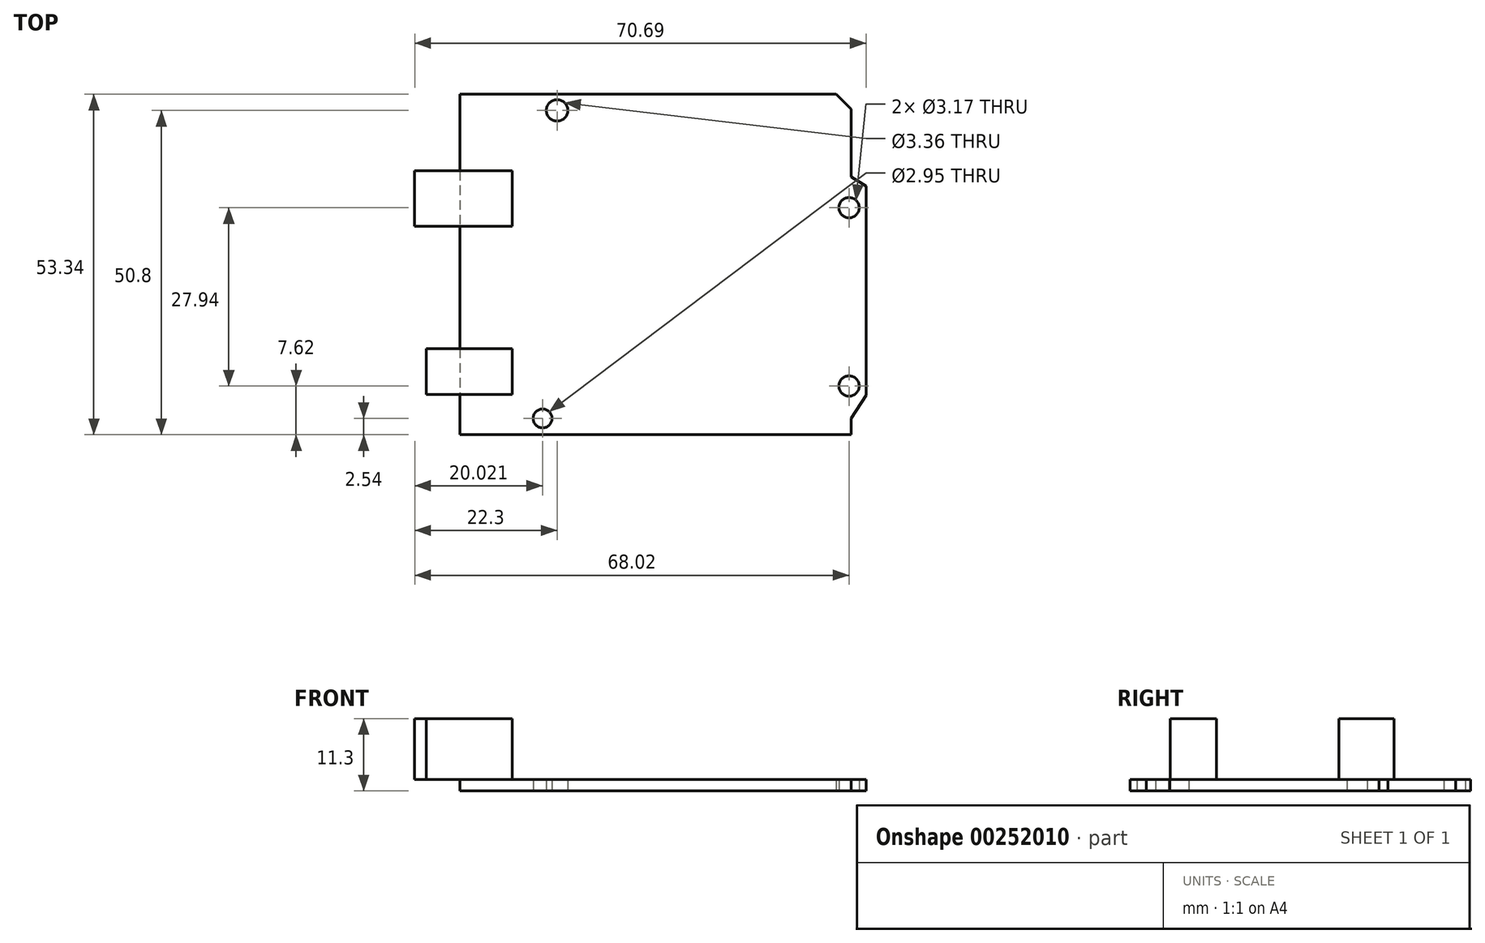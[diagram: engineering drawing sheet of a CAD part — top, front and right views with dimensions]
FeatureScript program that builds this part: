
annotation { "Feature Type Name" : "Feature", "Feature Type Description" : "" }
export const myFeature = defineFeature(function(context is Context, id is Id, definition is map)
    precondition{}
    {
        {
            var Q0;
            Q0=qCreatedBy(makeId("Top.planeOp"),FACE);
            var sketch = newSketch(context, id + "F0", { "sketchPlane" : qUnion([Q0])});
            skLineSegment(sketch, "E0", {"start": v(0, 0) * mm, "end": v(61.27, 0) * mm});
            skLineSegment(sketch, "E1", {"start": v(61.27, 0) * mm, "end": v(61.27, 2.54) * mm});
            skLineSegment(sketch, "E2", {"start": v(0, 53.34) * mm, "end": v(58.91, 53.34) * mm});
            skLineSegment(sketch, "E3", {"start": v(61.27, 50.98) * mm, "end": v(61.27, 40.38) * mm});
            skLineSegment(sketch, "E4", {"start": v(58.91, 53.34) * mm, "end": v(61.27, 50.98) * mm});
            skPoint(sketch, "E5", {"position": v(63.63, 38.97) * mm});
            skLineSegment(sketch, "E6", {"start": v(61.27, 40.38) * mm, "end": v(63.63, 38.97) * mm});
            skCircle(sketch, "E7", {"center": v(12.96, 2.54) * mm, "radius": 1.47 * mm});
            skCircle(sketch, "E8", {"center": v(15.24, 50.8) * mm, "radius": 1.68 * mm});
            skLineSegment(sketch, "E9", {"start": v(63.63, 38.97) * mm, "end": v(63.63, 6.2) * mm});
            skLineSegment(sketch, "E10", {"start": v(63.63, 6.2) * mm, "end": v(61.27, 2.54) * mm});
            skCircle(sketch, "E11", {"center": v(60.96, 35.56) * mm, "radius": 1.59 * mm});
            skCircle(sketch, "E12", {"center": v(60.96, 7.62) * mm, "radius": 1.59 * mm});
            skPoint(sketch, "E13.start.orphan", {"position": v(10.6, 2.95) * mm});
            skLineSegment(sketch, "E14", {"start": v(0, 53.34) * mm, "end": v(0, 0) * mm});
            skSolve(sketch);
        }
        {
            var Q0;
            Q0 = qSketchRegion(id + "F0", true);
            extrude(context, id + "F1", {"entities" : qUnion([Q0]), "depth" : 1.78 * mm});
        }
        {
            var Q0;
            Q0=makeQuery(id+"F1.opExtrude","CAP_FACE",FACE,{"disambiguationData":[OSD([sQuery(id+"F0.wireOp",EDGE,"E0"),sQuery(id+"F0.wireOp",EDGE,"E1"),sQuery(id+"F0.wireOp",EDGE,"E2"),sQuery(id+"F0.wireOp",EDGE,"E3"),sQuery(id+"F0.wireOp",EDGE,"E4"),sQuery(id+"F0.wireOp",EDGE,"E6"),sQuery(id+"F0.wireOp",EDGE,"E7"),sQuery(id+"F0.wireOp",EDGE,"E8"),sQuery(id+"F0.wireOp",EDGE,"E9"),sQuery(id+"F0.wireOp",EDGE,"E10"),sQuery(id+"F0.wireOp",EDGE,"E11"),sQuery(id+"F0.wireOp",EDGE,"E12"),sQuery(id+"F0.wireOp",EDGE,"E14")])],"isStart":false});
            var sketch = newSketch(context, id + "F2", { "sketchPlane" : qUnion([Q0])});
            skLineSegment(sketch, "E15.bottom", {"start": v(8.2, 41.34) * mm, "end": v(-7.06, 41.34) * mm});
            skLineSegment(sketch, "E15.top", {"start": v(8.2, 32.67) * mm, "end": v(-7.06, 32.67) * mm});
            skLineSegment(sketch, "E15.left", {"start": v(8.2, 41.34) * mm, "end": v(8.2, 32.67) * mm});
            skLineSegment(sketch, "E15.right", {"start": v(-7.06, 41.34) * mm, "end": v(-7.06, 32.67) * mm});
            skLineSegment(sketch, "E16.bottom", {"start": v(8.2, 13.5) * mm, "end": v(-5.23, 13.5) * mm});
            skLineSegment(sketch, "E16.top", {"start": v(8.2, 6.28) * mm, "end": v(-5.23, 6.28) * mm});
            skLineSegment(sketch, "E16.left", {"start": v(8.2, 13.5) * mm, "end": v(8.2, 6.28) * mm});
            skLineSegment(sketch, "E16.right", {"start": v(-5.23, 13.5) * mm, "end": v(-5.23, 6.28) * mm});
            skSolve(sketch);
        }
        {
            var Q0;
            {var subQ0=sQuery(id+"F2.wireOp",EDGE,"E15.right");Q0=makeQuery(id+"F2.imprint","IMPRINT",FACE,{"disambiguationData":[TD([[makeQuery(id+"F2.imprint","IMPRINT",EDGE,{"derivedFrom":subQ0}),1.0]])]});}
            var Q1;
            {var subQ0=sQuery(id+"F2.wireOp",EDGE,"E16.right");Q1=makeQuery(id+"F2.imprint","IMPRINT",FACE,{"disambiguationData":[TD([[makeQuery(id+"F2.imprint","IMPRINT",EDGE,{"derivedFrom":subQ0}),1.0]])]});}
            var Q2;
            {var subQ0=sQuery(id+"F2.wireOp",EDGE,"E15.left");Q2=makeQuery(id+"F2.imprint","IMPRINT",FACE,{"disambiguationData":[TD([[makeQuery(id+"F2.imprint","IMPRINT",EDGE,{"derivedFrom":subQ0}),-1.0]])]});}
            var Q3;
            {var subQ0=sQuery(id+"F2.wireOp",EDGE,"E16.left");Q3=makeQuery(id+"F2.imprint","IMPRINT",FACE,{"disambiguationData":[TD([[makeQuery(id+"F2.imprint","IMPRINT",EDGE,{"derivedFrom":subQ0}),-1.0]])]});}
            extrude(context, id + "F3", {"entities" : qUnion([Q0, Q1, Q2, Q3]), "depth" : 9.52 * mm});
        }
    });
